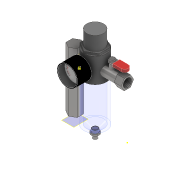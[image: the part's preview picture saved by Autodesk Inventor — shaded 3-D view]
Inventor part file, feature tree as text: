
AUTODESK INVENTOR PART (.ipt)
format: ipt  version: 2022 (Build 260153000, 153)  size: 441,856 bytes
history: native  units: mm
features: sketch x27, extrude x22, plane x5, split x2, thread x2, other x2, revolve x1, projected_geometry x1
ambient origin geometry x8: Origin, YZ Plane, XZ Plane, XY Plane, X Axis, Y Axis, Z Axis, Center Point
bodies: Solid1 (feature_tree), Solid6 (feature_tree), Solid7 (feature_tree), Solid8 (feature_tree), Solid9 (feature_tree), Solid10 (feature_tree), Solid2 (feature_tree), Solid3 (feature_tree), Solid4 (feature_tree), Solid5 (feature_tree)
feature tree (62):
  extrude  "Extrusion1"  Depth=85.0mm TaperAngle=0.0deg
  extrude  "Extrusion2"  Depth=3.0mm TaperAngle=0.0deg
  extrude  "Extrusion3"  Depth=10.0mm TaperAngle=0.0deg
  extrude  "Extrusion4"  Depth=3.0mm TaperAngle=0.0deg
  split  "Split1"
  split  "Split2"
  extrude  "Extrusion5"  Depth=20.0mm TaperAngle=0.0deg
  extrude  "Extrusion6"  Depth=10.0mm
  extrude  "Extrusion7"  Depth=10.0mm
  plane  "Work Plane1"
  extrude  "Extrusion8"  Depth=10.0mm TaperAngle=0.0deg
  sketch  "Sketch12"  dims[d40=8.0mm d41=0.0mm d42=20.0mm d43=0.0mm]
  plane  "Work Plane2"
  extrude  "Extrusion9"  Depth=4.5mm
  extrude  "Extrusion10"  TaperAngle=90.0deg  [1 undecoded]
  thread  "Thread1"  [1 undecoded]
  plane  "Work Plane3"
  extrude  "Extrusion11"  Depth=20.0mm TaperAngle=0.0deg
  revolve  "Revolution1"  [1 undecoded]
  extrude  "Extrusion12"  TaperAngle=0.0deg  [1 undecoded]
  plane  "Work Plane4"
  extrude  "Extrusion13"  Depth=7.0mm
  extrude  "Extrusion14"  Depth=4.0mm
  extrude  "Extrusion15"  Depth=6.0mm
  other  "Decal1"
  extrude  "Extrusion16"  Depth=10.949369mm
  extrude  "Extrusion17"  Depth=14.0mm
  plane  "Work Plane5"
  extrude  "Extrusion18"  Depth=8.0mm TaperAngle=0.0deg
  extrude  "Extrusion19"  Depth=26.679106mm
  extrude  "Extrusion20"  TaperAngle=90.0deg  [1 undecoded]
  extrude  "Extrusion21"  TaperAngle=90.0deg  [1 undecoded]
  thread  "Thread2"  [1 undecoded]
  extrude  "Extrusion22"  [1 undecoded]
  sketch  "Sketch1"  dims[d0=8.0mm d1=85.0mm d2=0.0mm]
  sketch  "Sketch2"  dims[d3=5.0mm d4=3.0mm d5=0.0mm]
  sketch  "Sketch3"  dims[d6=5.0mm d7=0.0mm d8=10.0mm d9=25.0mm d10=0.0mm d11=0.0mm]
  sketch  "Sketch4"  dims[d12=10.0mm d13=0.0mm d14=3.0mm d15=0.0mm]
  sketch  "Sketch6"  dims[d16=20.0mm d17=0.0mm d18=30.0mm d19=0.0mm]
  sketch  "Sketch7"  dims[d20=10.0mm d21=0.0mm d22=8.420912mm d23=14.0mm]
  sketch  "Sketch8"  dims[d24=12.25mm d25=10.0mm d26=0.0mm d27=0.0mm d28=12.0mm]
  sketch  "Sketch9"  dims[d29=10.0mm d30=0.0mm d31=10.0mm d32=0.0mm]
  sketch  "Sketch10"  dims[d33=-4.0mm d34=4.5mm]
  sketch  "Sketch11"  dims[d35=2.0mm d36=0.0mm d37=90.0deg d38=10.0mm d39=0.0mm]
  sketch  "Sketch13"  dims[d44=10.0mm d45=0.0mm d59=1.0mm d60=0.0mm]
  sketch  "Sketch14"  dims[d61=8.0mm d62=0.0mm d63=0.0mm]
  sketch  "Sketch15"  dims[d64=9.0mm d65=7.0mm]
  projected_geometry  "Projected Loop1"
  sketch  "Sketch16"  dims[d66=4.0mm d67=0.0mm d68=11.0mm]
  sketch  "Sketch17"  dims[d69=2.0mm d70=0.0mm d71=6.0mm]
  sketch  "Sketch19"  dims[d72=6.0mm d73=0.0mm d74=10.949369mm]
  sketch  "Sketch20"  dims[d76=14.0mm d77=14.0mm]
  sketch  "Sketch21"  dims[d78=3.0mm d79=0.0mm d80=8.0mm d81=0.0mm]
  sketch  "Sketch22"  dims[d82=29.041478mm d83=26.679106mm]
  other  "Image1"
  sketch  "Sketch23"  dims[d84=5.0mm d85=90.0deg]
  sketch  "Sketch24"  dims[d86=5.0mm d87=90.0deg d88=1.0mm d89=3.0mm d90=0.0mm d91=0.0mm]
  sketch  "Sketch25"
  sketch  "Sketch26"
  sketch  "Sketch27"
  sketch  "Sketch28"
  sketch  "Sketch29"
note: 8 required parameter values undecoded (feature->parameter linkage not recoverable at this tier; creation-order binding heuristic only, values carry confidence <= 0.55)